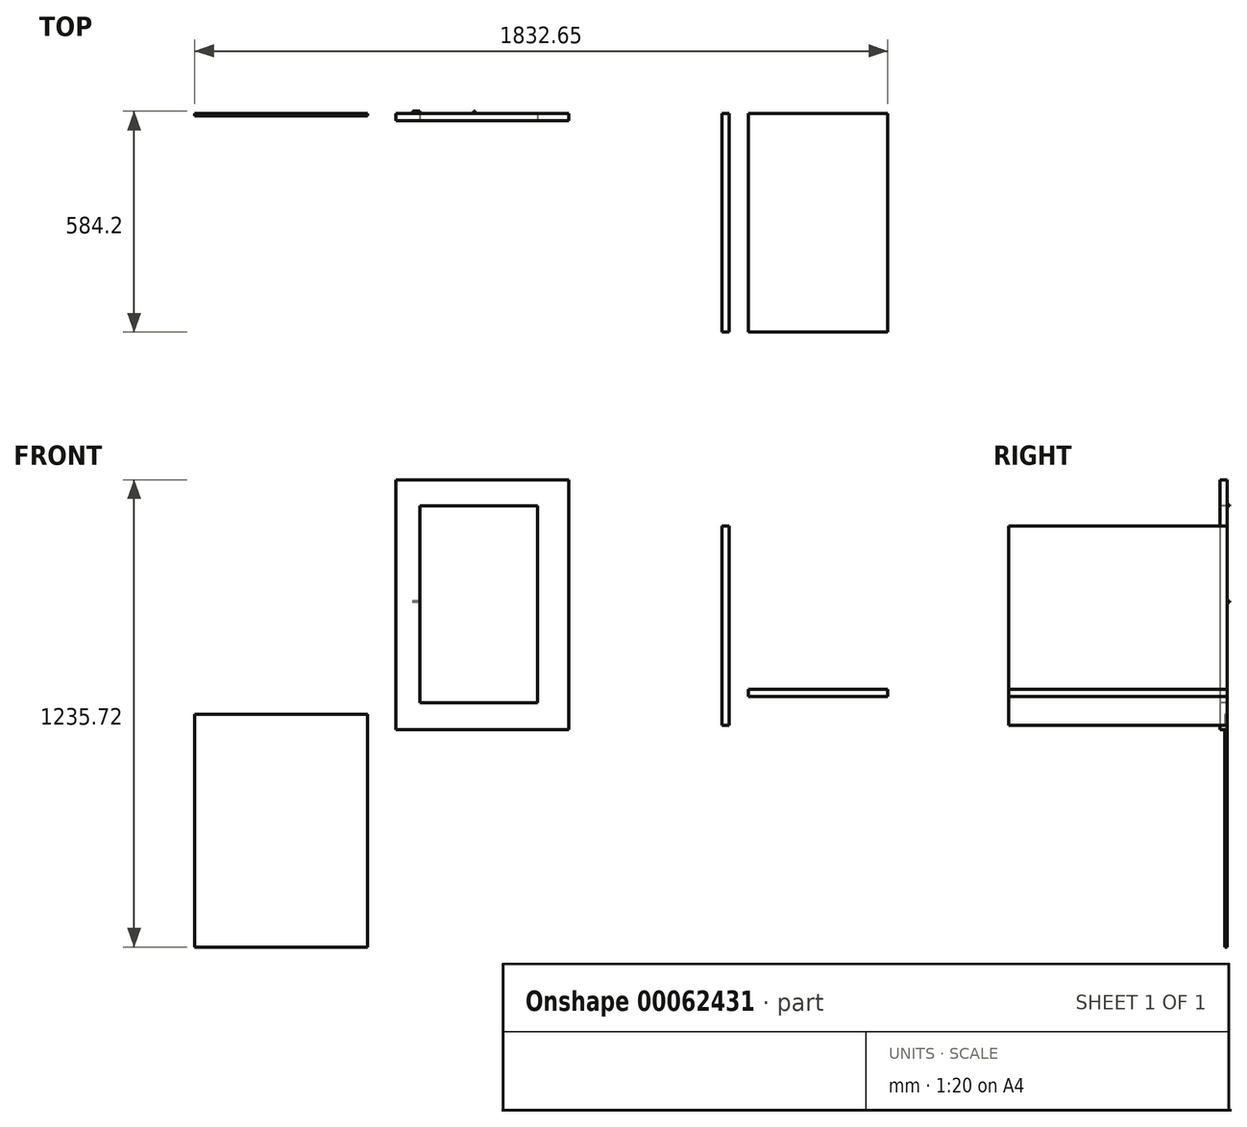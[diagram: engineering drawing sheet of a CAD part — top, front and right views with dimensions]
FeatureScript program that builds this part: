
annotation { "Feature Type Name" : "Feature", "Feature Type Description" : "" }
export const myFeature = defineFeature(function(context is Context, id is Id, definition is map)
    precondition{}
    {
        {
            var Q0;
            Q0=qCreatedBy(makeId("Front.planeOp"),FACE);
            var sketch = newSketch(context, id + "F0", { "sketchPlane" : qUnion([Q0])});
            skLineSegment(sketch, "E0.bottom", {"start": v(-69.6, 226) * mm, "end": v(-50.54, 226) * mm});
            skLineSegment(sketch, "E0.top", {"start": v(-69.6, -301.04) * mm, "end": v(-50.54, -301.04) * mm});
            skLineSegment(sketch, "E0.left", {"start": v(-69.6, 226) * mm, "end": v(-69.6, -301.04) * mm});
            skLineSegment(sketch, "E0.right", {"start": v(-50.54, 226) * mm, "end": v(-50.54, -301.04) * mm});
            skSolve(sketch);
        }
        {
            var Q0;
            Q0=qCreatedBy(makeId("Front.planeOp"),FACE);
            var sketch = newSketch(context, id + "F1", { "sketchPlane" : qUnion([Q0])});
            skLineSegment(sketch, "E1.bottom", {"start": v(0, -205.6) * mm, "end": v(368.3, -205.6) * mm});
            skLineSegment(sketch, "E1.top", {"start": v(0, -224.65) * mm, "end": v(368.3, -224.65) * mm});
            skLineSegment(sketch, "E1.left", {"start": v(0, -205.6) * mm, "end": v(0, -224.65) * mm});
            skLineSegment(sketch, "E1.right", {"start": v(368.3, -205.6) * mm, "end": v(368.3, -224.65) * mm});
            skSolve(sketch);
        }
        {
            var Q0;
            Q0 = qSketchRegion(id + "F1", true);
            extrude(context, id + "F2", {"entities" : qUnion([Q0]), "depth" : 577.85 * mm});
        }
        {
            var Q0;
            Q0 = qSketchRegion(id + "F0", true);
            extrude(context, id + "F3", {"entities" : qUnion([Q0]), "depth" : 577.85 * mm});
        }
        {
            var Q0;
            Q0=qCreatedBy(makeId("Front.planeOp"),FACE);
            var sketch = newSketch(context, id + "F4", { "sketchPlane" : qUnion([Q0])});
            skLineSegment(sketch, "E2.bottom", {"start": v(-1464.35, -271.3) * mm, "end": v(-1007.15, -271.3) * mm});
            skLineSegment(sketch, "E2.top", {"start": v(-1464.35, -887.25) * mm, "end": v(-1007.15, -887.25) * mm});
            skLineSegment(sketch, "E2.left", {"start": v(-1464.35, -271.3) * mm, "end": v(-1464.35, -887.25) * mm});
            skLineSegment(sketch, "E2.right", {"start": v(-1007.15, -271.3) * mm, "end": v(-1007.15, -887.25) * mm});
            skSolve(sketch);
        }
        {
            var Q0;
            Q0 = qSketchRegion(id + "F4", true);
            extrude(context, id + "F5", {"entities" : qUnion([Q0]), "depth" : 6.35 * mm});
        }
        {
            var Q0;
            Q0=qCreatedBy(makeId("Front.planeOp"),FACE);
            var sketch = newSketch(context, id + "F6", { "sketchPlane" : qUnion([Q0])});
            skLineSegment(sketch, "E3.bottom", {"start": v(-932.08, 348.47) * mm, "end": v(-474.88, 348.47) * mm});
            skLineSegment(sketch, "E3.top", {"start": v(-932.08, -311.93) * mm, "end": v(-474.88, -311.93) * mm});
            skLineSegment(sketch, "E3.left", {"start": v(-932.08, 348.47) * mm, "end": v(-932.08, -311.93) * mm});
            skLineSegment(sketch, "E3.right", {"start": v(-474.88, 348.47) * mm, "end": v(-474.88, -311.93) * mm});
            skSolve(sketch);
        }
        {
            var Q0;
            Q0 = qSketchRegion(id + "F6", true);
            extrude(context, id + "F7", {"entities" : qUnion([Q0]), "depth" : 19.05 * mm});
        }
        {
            var Q0;
            Q0=makeQuery(id+"F7.opExtrude","CAP_FACE",FACE,{"disambiguationData":[OSD([sQuery(id+"F6.wireOp",EDGE,"E3.bottom"),sQuery(id+"F6.wireOp",EDGE,"E3.top"),sQuery(id+"F6.wireOp",EDGE,"E3.left"),sQuery(id+"F6.wireOp",EDGE,"E3.right")])],"isStart":false});
            var sketch = newSketch(context, id + "F8", { "sketchPlane" : qUnion([Q0])});
            skLineSegment(sketch, "E4.bottom", {"start": v(-868.58, 278.88) * mm, "end": v(-557.43, 278.88) * mm});
            skLineSegment(sketch, "E4.top", {"start": v(-868.58, -241.82) * mm, "end": v(-557.43, -241.82) * mm});
            skLineSegment(sketch, "E4.left", {"start": v(-868.58, 278.88) * mm, "end": v(-868.58, -241.82) * mm});
            skLineSegment(sketch, "E4.right", {"start": v(-557.43, 278.88) * mm, "end": v(-557.43, -241.82) * mm});
            skSolve(sketch);
        }
        {
            var Q0;
            Q0=makeQuery(id+"F8.imprint","IMPRINT",FACE,{"disambiguationData":[TD([[makeQuery(id+"F8.imprint","IMPRINT",EDGE,{"derivedFrom":sQuery(id+"F8.wireOp",EDGE,"E4.bottom")}),-1.0]])]});
            extrude(context, id + "F9", {"entities" : qUnion([Q0]), "operationType" : NewBodyOperationType.REMOVE, "oppositeDirection" : true, "depth" : 25.4 * mm});
        }
        {
            var Q0;
            Q0=makeQuery(id+"F7.opExtrude","CAP_FACE",FACE,{"disambiguationData":[OSD([sQuery(id+"F6.wireOp",EDGE,"E3.bottom"),sQuery(id+"F6.wireOp",EDGE,"E3.top"),sQuery(id+"F6.wireOp",EDGE,"E3.left"),sQuery(id+"F6.wireOp",EDGE,"E3.right")])],"isStart":true});
            var sketch = newSketch(context, id + "F10", { "sketchPlane" : qUnion([Q0])});
            skLineSegment(sketch, "E5.bottom", {"start": v(868.58, 27.73) * mm, "end": v(887.63, 27.73) * mm});
            skLineSegment(sketch, "E5.top", {"start": v(868.58, 24.04) * mm, "end": v(887.63, 24.04) * mm});
            skLineSegment(sketch, "E5.left", {"start": v(868.58, 27.73) * mm, "end": v(868.58, 24.04) * mm});
            skLineSegment(sketch, "E5.right", {"start": v(887.63, 27.73) * mm, "end": v(887.63, 24.04) * mm});
            skSolve(sketch);
        }
        {
            var Q0;
            Q0 = qSketchRegion(id + "F10", true);
            extrude(context, id + "F11", {"entities" : qUnion([Q0]), "operationType" : NewBodyOperationType.ADD, "depth" : 6.35 * mm});
        }
        {
            var Q0;
            Q0=makeQuery(id+"F7.opExtrude","CAP_FACE",FACE,{"disambiguationData":[OSD([sQuery(id+"F6.wireOp",EDGE,"E3.bottom"),sQuery(id+"F6.wireOp",EDGE,"E3.top"),sQuery(id+"F6.wireOp",EDGE,"E3.left"),sQuery(id+"F6.wireOp",EDGE,"E3.right")])],"isStart":true});
            var sketch = newSketch(context, id + "F12", { "sketchPlane" : qUnion([Q0])});
            skLineSegment(sketch, "E6.bottom", {"start": v(726.73, 278.88) * mm, "end": v(722.31, 278.88) * mm});
            skLineSegment(sketch, "E6.top", {"start": v(726.73, 282.05) * mm, "end": v(722.31, 282.05) * mm});
            skLineSegment(sketch, "E6.left", {"start": v(726.73, 278.88) * mm, "end": v(726.73, 282.05) * mm});
            skLineSegment(sketch, "E6.right", {"start": v(722.31, 278.88) * mm, "end": v(722.31, 282.05) * mm});
            skSolve(sketch);
        }
        {
            var Q0;
            Q0 = qSketchRegion(id + "F12", true);
            extrude(context, id + "F13", {"entities" : qUnion([Q0]), "operationType" : NewBodyOperationType.ADD, "depth" : 6.35 * mm});
        }
        {
            var Q0;
            Q0=makeQuery(id+"F2.opExtrude","SWEPT_BODY",BODY,{"disambiguationData":[OSD([sQuery(id+"F1.wireOp",EDGE,"E1.bottom"),sQuery(id+"F1.wireOp",EDGE,"E1.top"),sQuery(id+"F1.wireOp",EDGE,"E1.left"),sQuery(id+"F1.wireOp",EDGE,"E1.right")])]});
            transform(context, id + "F14", {"entities" : qUnion([Q0]), "transformType" : TransformType.TRANSLATION_3D, "dx" : 0 * mm, "dy" : 0 * mm, "dz" : 0 * mm, "makeCopy" : true});
        }
        {
            var Q0;
            Q0=makeQuery(id+"F2.opExtrude","SWEPT_BODY",BODY,{"disambiguationData":[OSD([sQuery(id+"F1.wireOp",EDGE,"E1.bottom"),sQuery(id+"F1.wireOp",EDGE,"E1.top"),sQuery(id+"F1.wireOp",EDGE,"E1.left"),sQuery(id+"F1.wireOp",EDGE,"E1.right")])]});
            transform(context, id + "F15", {"entities" : qUnion([Q0]), "transformType" : TransformType.TRANSLATION_3D, "dx" : 0 * mm, "dy" : 0 * mm, "dz" : 0 * mm, "makeCopy" : true});
        }
    });
